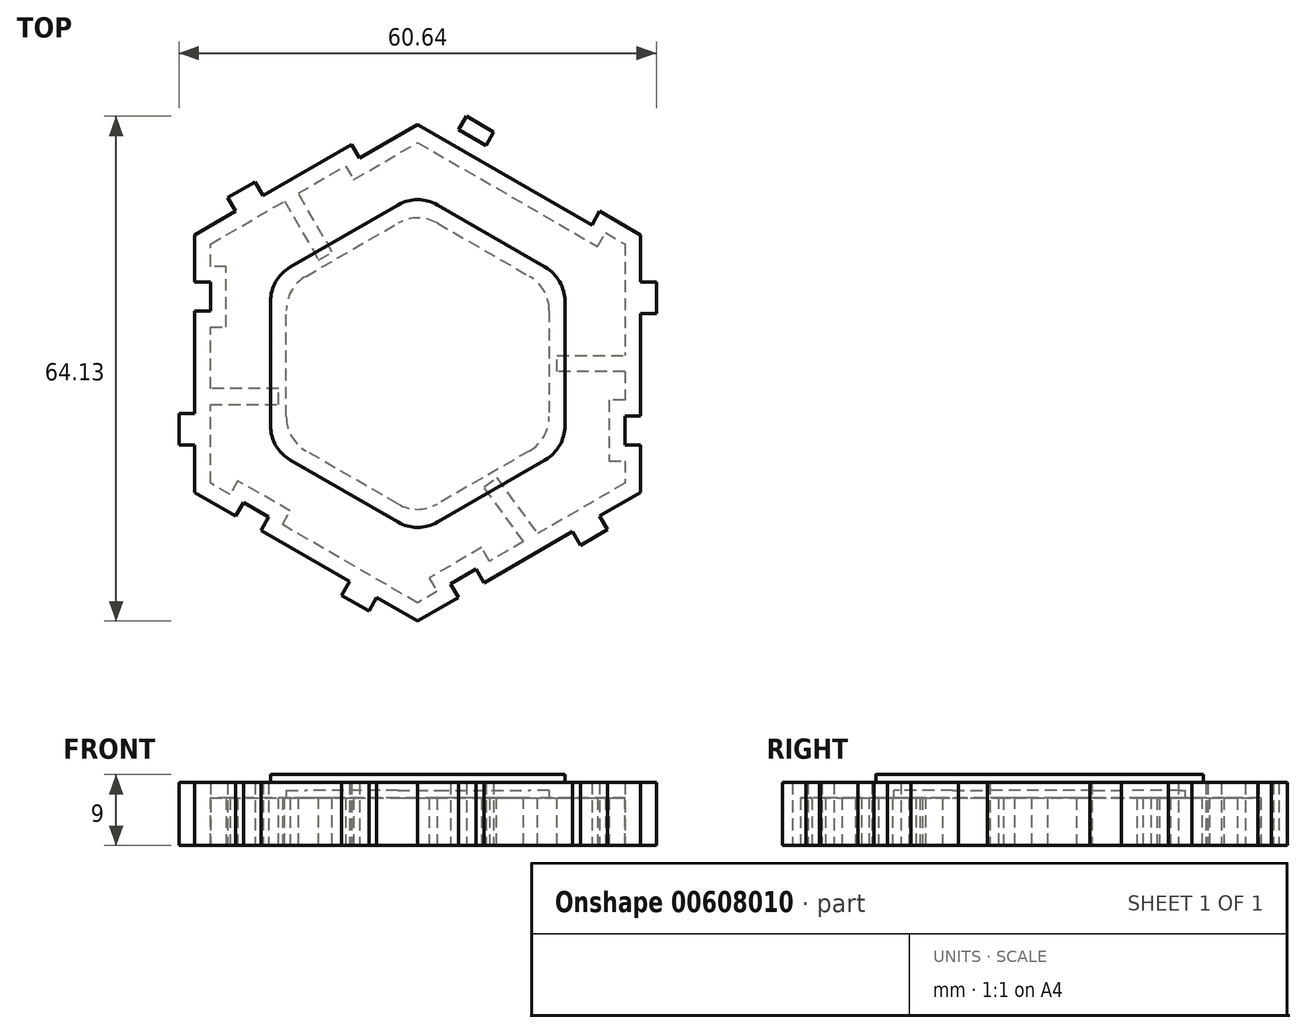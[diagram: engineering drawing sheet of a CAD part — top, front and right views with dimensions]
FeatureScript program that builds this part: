
annotation { "Feature Type Name" : "Feature", "Feature Type Description" : "" }
export const myFeature = defineFeature(function(context is Context, id is Id, definition is map)
    precondition{}
    {
        {
            var Q0;
            Q0=qCreatedBy(makeId("Top.planeOp"),FACE);
            var sketch = newSketch(context, id + "F0", { "sketchPlane" : qUnion([Q0])});
            skCircle(sketch, "E0.cCircle", {"center": v(0, 0) * mm, "radius": 18.7 * mm, "construction": true});
            skLineSegment(sketch, "E0.0", {"start": v(-18.7, -10.8) * mm, "end": v(-18.7, 10.8) * mm});
            skLineSegment(sketch, "E0.1", {"start": v(-18.7, 10.8) * mm, "end": v(0, 21.6) * mm});
            skLineSegment(sketch, "E0.2", {"start": v(0, 21.6) * mm, "end": v(18.7, 10.8) * mm});
            skLineSegment(sketch, "E0.3", {"start": v(18.7, 10.8) * mm, "end": v(18.7, -10.8) * mm});
            skLineSegment(sketch, "E0.4", {"start": v(18.7, -10.8) * mm, "end": v(0, -21.6) * mm});
            skLineSegment(sketch, "E0.5", {"start": v(0, -21.6) * mm, "end": v(-18.7, -10.8) * mm});
            skPoint(sketch, "E0.0.midPoint", {"position": v(-18.7, 0) * mm});
            skLineSegment(sketch, "E1.0", {"start": v(-26.32, 15.2) * mm, "end": v(0, 30.39) * mm});
            skLineSegment(sketch, "E1.1", {"start": v(26.32, 15.2) * mm, "end": v(26.32, -15.2) * mm});
            skLineSegment(sketch, "E1.2", {"start": v(26.32, -15.2) * mm, "end": v(0, -30.39) * mm});
            skLineSegment(sketch, "E1.3", {"start": v(0, 30.39) * mm, "end": v(26.32, 15.2) * mm});
            skLineSegment(sketch, "E1.4", {"start": v(0, -30.39) * mm, "end": v(-26.32, -15.2) * mm});
            skLineSegment(sketch, "E1.5", {"start": v(-26.32, -15.2) * mm, "end": v(-26.32, 15.2) * mm});
            skLineSegment(sketch, "E2.0", {"start": v(-28.32, 16.35) * mm, "end": v(0, 32.7) * mm});
            skLineSegment(sketch, "E2.1", {"start": v(28.32, 16.35) * mm, "end": v(28.32, -16.35) * mm});
            skLineSegment(sketch, "E2.2", {"start": v(28.32, -16.35) * mm, "end": v(0, -32.7) * mm});
            skLineSegment(sketch, "E2.3", {"start": v(0, 32.7) * mm, "end": v(28.32, 16.35) * mm});
            skLineSegment(sketch, "E2.4", {"start": v(0, -32.7) * mm, "end": v(-28.32, -16.35) * mm});
            skLineSegment(sketch, "E2.5", {"start": v(-28.32, -16.35) * mm, "end": v(-28.32, 16.35) * mm});
            skLineSegment(sketch, "E3", {"start": v(-23.12, 19.35) * mm, "end": v(-24.12, 21.08) * mm});
            skLineSegment(sketch, "E4", {"start": v(-24.12, 21.08) * mm, "end": v(-20.66, 23.08) * mm});
            skLineSegment(sketch, "E5", {"start": v(-20.66, 23.08) * mm, "end": v(-19.66, 21.35) * mm});
            skLineSegment(sketch, "E6", {"start": v(-8.4, 27.85) * mm, "end": v(-7.4, 26.12) * mm});
            skLineSegment(sketch, "E7", {"start": v(-7.4, 26.12) * mm, "end": v(-4.2, 27.97) * mm});
            skLineSegment(sketch, "E8", {"start": v(-4.2, 27.97) * mm, "end": v(-5.2, 29.7) * mm});
            skLineSegment(sketch, "E9.1.0", {"start": v(30.32, 10.35) * mm, "end": v(30.32, 6.35) * mm});
            skLineSegment(sketch, "E9.1.1", {"start": v(30.32, 6.35) * mm, "end": v(28.32, 6.35) * mm});
            skLineSegment(sketch, "E9.1.2", {"start": v(28.32, -6.65) * mm, "end": v(26.32, -6.65) * mm});
            skLineSegment(sketch, "E9.1.3", {"start": v(26.32, -10.35) * mm, "end": v(28.32, -10.35) * mm});
            skLineSegment(sketch, "E9.1.4", {"start": v(28.32, 10.35) * mm, "end": v(30.32, 10.35) * mm});
            skLineSegment(sketch, "E9.2.0", {"start": v(-6.2, -31.43) * mm, "end": v(-9.66, -29.43) * mm});
            skLineSegment(sketch, "E9.2.1", {"start": v(-9.66, -29.43) * mm, "end": v(-8.66, -27.7) * mm});
            skLineSegment(sketch, "E9.2.2", {"start": v(-19.92, -21.2) * mm, "end": v(-18.92, -19.47) * mm});
            skLineSegment(sketch, "E9.2.3", {"start": v(-22.12, -17.62) * mm, "end": v(-23.12, -19.35) * mm});
            skLineSegment(sketch, "E9.2.4", {"start": v(-5.2, -29.7) * mm, "end": v(-6.2, -31.43) * mm});
            skLineSegment(sketch, "E9.anchor1", {"start": v(0, 0) * mm, "end": v(-24.12, 21.08) * mm, "construction": true});
            skLineSegment(sketch, "E9.anchor2", {"start": v(0, 0) * mm, "end": v(-6.2, -31.43) * mm, "construction": true});
            skLineSegment(sketch, "E10.1.0", {"start": v(-30.32, -6.35) * mm, "end": v(-28.32, -6.35) * mm});
            skLineSegment(sketch, "E10.1.1", {"start": v(-30.32, -10.35) * mm, "end": v(-30.32, -6.35) * mm});
            skLineSegment(sketch, "E10.1.2", {"start": v(-28.32, -10.35) * mm, "end": v(-30.32, -10.35) * mm});
            skLineSegment(sketch, "E10.1.3", {"start": v(-28.32, 6.65) * mm, "end": v(-26.32, 6.65) * mm});
            skLineSegment(sketch, "E10.1.4", {"start": v(-26.32, 10.35) * mm, "end": v(-28.32, 10.35) * mm});
            skLineSegment(sketch, "E10.anchor1", {"start": v(0, 0) * mm, "end": v(-9.66, -29.43) * mm, "construction": true});
            skLineSegment(sketch, "E10.anchor2", {"start": v(0, 0) * mm, "end": v(-20.66, 23.08) * mm, "construction": true});
            skLineSegment(sketch, "E11.1.0", {"start": v(23.12, -19.35) * mm, "end": v(24.12, -21.08) * mm});
            skLineSegment(sketch, "E11.1.1", {"start": v(20.66, -23.08) * mm, "end": v(19.66, -21.35) * mm});
            skLineSegment(sketch, "E11.1.2", {"start": v(24.12, -21.08) * mm, "end": v(20.66, -23.08) * mm});
            skLineSegment(sketch, "E11.1.3", {"start": v(8.4, -27.85) * mm, "end": v(7.4, -26.12) * mm});
            skLineSegment(sketch, "E11.1.4", {"start": v(4.2, -27.97) * mm, "end": v(5.2, -29.7) * mm});
            skLineSegment(sketch, "E11.anchor1", {"start": v(0, 0) * mm, "end": v(28.32, 10.35) * mm, "construction": true});
            skLineSegment(sketch, "E11.anchor2", {"start": v(0, 0) * mm, "end": v(-5.2, -29.7) * mm, "construction": true});
            skLineSegment(sketch, "E12.1.0", {"start": v(22.12, 17.62) * mm, "end": v(23.12, 19.35) * mm});
            skLineSegment(sketch, "E12.1.1", {"start": v(19.92, 21.2) * mm, "end": v(18.92, 19.47) * mm});
            skLineSegment(sketch, "E12.1.2", {"start": v(9.66, 29.43) * mm, "end": v(8.66, 27.7) * mm});
            skLineSegment(sketch, "E12.1.3", {"start": v(6.2, 31.43) * mm, "end": v(9.66, 29.43) * mm});
            skLineSegment(sketch, "E12.1.4", {"start": v(5.2, 29.7) * mm, "end": v(6.2, 31.43) * mm});
            skLineSegment(sketch, "E12.anchor1", {"start": v(0, 0) * mm, "end": v(-28.32, 10.35) * mm, "construction": true});
            skLineSegment(sketch, "E12.anchor2", {"start": v(0, 0) * mm, "end": v(5.2, -29.7) * mm, "construction": true});
            skSolve(sketch);
        }
        {
            var Q0;
            {var subQ0=sQuery(id+"F0.wireOp",EDGE,"E3");Q0=makeQuery(id+"F0.imprint","IMPRINT",FACE,{"disambiguationData":[TD([[makeQuery(id+"F0.imprint","IMPRINT",EDGE,{"derivedFrom":subQ0}),-1.0]])]});}
            var Q1;
            Q1=makeQuery(id+"F0.imprint","IMPRINT",FACE,{"disambiguationData":[TD([[makeQuery(id+"F0.imprint","IMPRINT",EDGE,{"derivedFrom":sQuery(id+"F0.wireOp",EDGE,"E0.0")}),1.0]])]});
            var Q2;
            Q2=makeQuery(id+"F0.imprint","IMPRINT",FACE,{"disambiguationData":[TD([[makeQuery(id+"F0.imprint","IMPRINT",EDGE,{"derivedFrom":sQuery(id+"F0.wireOp",EDGE,"E9.2.0")}),-1.0]])]});
            var Q3;
            Q3=makeQuery(id+"F0.imprint","IMPRINT",FACE,{"disambiguationData":[TD([[makeQuery(id+"F0.imprint","IMPRINT",EDGE,{"derivedFrom":sQuery(id+"F0.wireOp",EDGE,"E9.1.0")}),-1.0]])]});
            var Q4;
            {var subQ0=sQuery(id+"F0.wireOp",EDGE,"E10.1.0");Q4=makeQuery(id+"F0.imprint","IMPRINT",FACE,{"disambiguationData":[TD([[makeQuery(id+"F0.imprint","IMPRINT",EDGE,{"derivedFrom":subQ0}),-1.0]])]});}
            var Q5;
            {var subQ9=sQuery(id+"F0.wireOp",EDGE,"E9.2.3");Q5=makeQuery(id+"F0.imprint","IMPRINT",FACE,{"disambiguationData":[TD([[makeQuery(id+"F0.imprint","IMPRINT",EDGE,{"derivedFrom":subQ9}),-1.0]])]});}
            var Q6;
            {var subQ8=sQuery(id+"F0.wireOp",EDGE,"E10.1.4");Q6=makeQuery(id+"F0.imprint","IMPRINT",FACE,{"disambiguationData":[TD([[makeQuery(id+"F0.imprint","IMPRINT",EDGE,{"derivedFrom":subQ8}),-1.0]])]});}
            var Q7;
            {var subQ0=sQuery(id+"F0.wireOp",EDGE,"E5");Q7=makeQuery(id+"F0.imprint","IMPRINT",FACE,{"disambiguationData":[TD([[makeQuery(id+"F0.imprint","IMPRINT",EDGE,{"derivedFrom":subQ0}),-1.0]])]});}
            var Q8;
            {var subQ7=sQuery(id+"F0.wireOp",EDGE,"E10.1.3");Q8=makeQuery(id+"F0.imprint","IMPRINT",FACE,{"disambiguationData":[TD([[makeQuery(id+"F0.imprint","IMPRINT",EDGE,{"derivedFrom":subQ7}),-1.0]])]});}
            var Q9;
            {var subQ8=sQuery(id+"F0.wireOp",EDGE,"E11.1.4");Q9=makeQuery(id+"F0.imprint","IMPRINT",FACE,{"disambiguationData":[TD([[makeQuery(id+"F0.imprint","IMPRINT",EDGE,{"derivedFrom":subQ8}),-1.0]])]});}
            var Q10;
            {var subQ0=sQuery(id+"F0.wireOp",EDGE,"E9.2.4");Q10=makeQuery(id+"F0.imprint","IMPRINT",FACE,{"disambiguationData":[TD([[makeQuery(id+"F0.imprint","IMPRINT",EDGE,{"derivedFrom":subQ0}),-1.0]])]});}
            var Q11;
            {var subQ9=sQuery(id+"F0.wireOp",EDGE,"E9.1.3");Q11=makeQuery(id+"F0.imprint","IMPRINT",FACE,{"disambiguationData":[TD([[makeQuery(id+"F0.imprint","IMPRINT",EDGE,{"derivedFrom":subQ9}),-1.0]])]});}
            var Q12;
            {var subQ0=sQuery(id+"F0.wireOp",EDGE,"E11.1.0");Q12=makeQuery(id+"F0.imprint","IMPRINT",FACE,{"disambiguationData":[TD([[makeQuery(id+"F0.imprint","IMPRINT",EDGE,{"derivedFrom":subQ0}),-1.0]])]});}
            var Q13;
            {var subQ4=sQuery(id+"F0.wireOp",EDGE,"E8");Q13=makeQuery(id+"F0.imprint","IMPRINT",FACE,{"disambiguationData":[TD([[makeQuery(id+"F0.imprint","IMPRINT",EDGE,{"derivedFrom":subQ4}),-1.0]])]});}
            var Q14;
            {var subQ0=sQuery(id+"F0.wireOp",EDGE,"E12.1.2");Q14=makeQuery(id+"F0.imprint","IMPRINT",FACE,{"disambiguationData":[TD([[makeQuery(id+"F0.imprint","IMPRINT",EDGE,{"derivedFrom":subQ0}),-1.0]])]});}
            var Q15;
            {var subQ9=sQuery(id+"F0.wireOp",EDGE,"E9.1.2");Q15=makeQuery(id+"F0.imprint","IMPRINT",FACE,{"disambiguationData":[TD([[makeQuery(id+"F0.imprint","IMPRINT",EDGE,{"derivedFrom":subQ9}),-1.0]])]});}
            var Q16;
            {var subQ7=sQuery(id+"F0.wireOp",EDGE,"E9.2.2");Q16=makeQuery(id+"F0.imprint","IMPRINT",FACE,{"disambiguationData":[TD([[makeQuery(id+"F0.imprint","IMPRINT",EDGE,{"derivedFrom":subQ7}),-1.0]])]});}
            var Q17;
            {var subQ0=sQuery(id+"F0.wireOp",EDGE,"E11.1.1");Q17=makeQuery(id+"F0.imprint","IMPRINT",FACE,{"disambiguationData":[TD([[makeQuery(id+"F0.imprint","IMPRINT",EDGE,{"derivedFrom":subQ0}),-1.0]])]});}
            extrude(context, id + "F1", {"entities" : qUnion([Q0, Q1, Q2, Q3, Q4, Q5, Q6, Q7, Q8, Q9, Q10, Q11, Q12, Q13, Q14, Q15, Q16, Q17]), "depth" : 8 * mm, "offsetDistance" : 25 * mm});
        }
        {
            var Q0;
            Q0=makeQuery(id+"F0.imprint","IMPRINT",FACE,{"disambiguationData":[TD([[makeQuery(id+"F0.imprint","IMPRINT",EDGE,{"derivedFrom":sQuery(id+"F0.wireOp",EDGE,"E0.0")}),-1.0]])]});
            extrude(context, id + "F2", {"entities" : qUnion([Q0]), "operationType" : NewBodyOperationType.ADD, "depth" : 9 * mm, "offsetDistance" : 25 * mm});
        }
        {
            var Q0;
            {var subQ0=sQuery(id+"F0.wireOp",EDGE,"E0.5");var subQ1=sQuery(id+"F0.wireOp",EDGE,"E0.4");var subQ2=sQuery(id+"F0.wireOp",EDGE,"E0.3");var subQ3=sQuery(id+"F0.wireOp",EDGE,"E0.2");var subQ4=sQuery(id+"F0.wireOp",EDGE,"E0.1");var subQ5=sQuery(id+"F0.wireOp",EDGE,"E0.0");Q0=makeQuery(id+"F2.boolean.opBoolean","MERGE",FACE,{"derivedFrom":[makeQuery(id+"F1.opExtrude","CAP_FACE",FACE,{"disambiguationData":[OSD([subQ5,subQ4,subQ3,subQ2,subQ1,subQ0,sQuery(id+"F0.wireOp",EDGE,"E1.1"),sQuery(id+"F0.wireOp",EDGE,"E1.2"),sQuery(id+"F0.wireOp",EDGE,"E1.3"),sQuery(id+"F0.wireOp",EDGE,"E1.4"),sQuery(id+"F0.wireOp",EDGE,"E1.5"),sQuery(id+"F0.wireOp",EDGE,"E2.0"),sQuery(id+"F0.wireOp",EDGE,"E2.1"),sQuery(id+"F0.wireOp",EDGE,"E2.2"),sQuery(id+"F0.wireOp",EDGE,"E2.3"),sQuery(id+"F0.wireOp",EDGE,"E2.4"),sQuery(id+"F0.wireOp",EDGE,"E2.5"),sQuery(id+"F0.wireOp",EDGE,"E7"),sQuery(id+"F0.wireOp",EDGE,"E9.1.0"),sQuery(id+"F0.wireOp",EDGE,"E9.1.1"),sQuery(id+"F0.wireOp",EDGE,"E9.1.2"),sQuery(id+"F0.wireOp",EDGE,"E9.1.3"),sQuery(id+"F0.wireOp",EDGE,"E9.1.4"),sQuery(id+"F0.wireOp",EDGE,"E10.1.0"),sQuery(id+"F0.wireOp",EDGE,"E10.1.1"),sQuery(id+"F0.wireOp",EDGE,"E10.1.2"),sQuery(id+"F0.wireOp",EDGE,"E10.1.3"),sQuery(id+"F0.wireOp",EDGE,"E10.1.4"),sQuery(id+"F0.wireOp",EDGE,"E5"),sQuery(id+"F0.wireOp",EDGE,"E4"),sQuery(id+"F0.wireOp",EDGE,"E3"),sQuery(id+"F0.wireOp",EDGE,"E6"),sQuery(id+"F0.wireOp",EDGE,"E8"),sQuery(id+"F0.wireOp",EDGE,"E9.2.4"),sQuery(id+"F0.wireOp",EDGE,"E9.2.1"),sQuery(id+"F0.wireOp",EDGE,"E9.2.0"),sQuery(id+"F0.wireOp",EDGE,"E9.2.2"),sQuery(id+"F0.wireOp",EDGE,"E9.2.3"),sQuery(id+"F0.wireOp",EDGE,"E12.1.0"),sQuery(id+"F0.wireOp",EDGE,"E12.1.1"),sQuery(id+"F0.wireOp",EDGE,"E12.1.2"),sQuery(id+"F0.wireOp",EDGE,"E12.1.3"),sQuery(id+"F0.wireOp",EDGE,"E12.1.4"),sQuery(id+"F0.wireOp",EDGE,"E11.1.4"),sQuery(id+"F0.wireOp",EDGE,"E11.1.3"),sQuery(id+"F0.wireOp",EDGE,"E11.1.1"),sQuery(id+"F0.wireOp",EDGE,"E11.1.2"),sQuery(id+"F0.wireOp",EDGE,"E11.1.0")])],"isStart":true}),makeQuery(id+"F2.opExtrude","CAP_FACE",FACE,{"disambiguationData":[OSD([subQ5,subQ4,subQ3,subQ2,subQ1,subQ0])],"isStart":true})]});}
            shell(context, id + "F3", {"entities" : qUnion([Q0]), "thickness" : 2 * mm});
        }
        {
            var Q0;
            Q0=makeQuery(id+"F2.opExtrude","SWEPT_EDGE",EDGE,{"disambiguationData":[OSD([sQuery(id+"F0.wireOp",EDGE,"E0.0"),sQuery(id+"F0.wireOp",EDGE,"E0.1")])]});
            var Q1;
            Q1=makeQuery(id+"F2.opExtrude","SWEPT_EDGE",EDGE,{"disambiguationData":[OSD([sQuery(id+"F0.wireOp",EDGE,"E0.0"),sQuery(id+"F0.wireOp",EDGE,"E0.5")])]});
            var Q2;
            Q2=makeQuery(id+"F2.opExtrude","SWEPT_EDGE",EDGE,{"disambiguationData":[OSD([sQuery(id+"F0.wireOp",EDGE,"E0.4"),sQuery(id+"F0.wireOp",EDGE,"E0.5")])]});
            var Q3;
            Q3=makeQuery(id+"F2.opExtrude","SWEPT_EDGE",EDGE,{"disambiguationData":[OSD([sQuery(id+"F0.wireOp",EDGE,"E0.3"),sQuery(id+"F0.wireOp",EDGE,"E0.4")])]});
            var Q4;
            Q4=makeQuery(id+"F2.opExtrude","SWEPT_EDGE",EDGE,{"disambiguationData":[OSD([sQuery(id+"F0.wireOp",EDGE,"E0.2"),sQuery(id+"F0.wireOp",EDGE,"E0.3")])]});
            var Q5;
            Q5=makeQuery(id+"F2.opExtrude","SWEPT_EDGE",EDGE,{"disambiguationData":[OSD([sQuery(id+"F0.wireOp",EDGE,"E0.1"),sQuery(id+"F0.wireOp",EDGE,"E0.2")])]});
            fillet(context, id + "F4", {"entities" : qUnion([Q0, Q1, Q2, Q3, Q4, Q5]), "radius" : 5 * mm, "tangentPropagation" : true, "allowEdgeOverflow" : false});
        }
        {
            var Q0;
            Q0=makeQuery(id+"F3.opShell","OFFSET_EDGE",EDGE,{"disambiguationData":[OSD([sQuery(id+"F0.wireOp",EDGE,"E0.1"),sQuery(id+"F0.wireOp",EDGE,"E0.2")])]});
            var Q1;
            Q1=makeQuery(id+"F3.opShell","OFFSET_EDGE",EDGE,{"disambiguationData":[OSD([sQuery(id+"F0.wireOp",EDGE,"E0.0"),sQuery(id+"F0.wireOp",EDGE,"E0.1")])]});
            var Q2;
            Q2=makeQuery(id+"F3.opShell","OFFSET_EDGE",EDGE,{"disambiguationData":[OSD([sQuery(id+"F0.wireOp",EDGE,"E0.0"),sQuery(id+"F0.wireOp",EDGE,"E0.5")])]});
            var Q3;
            Q3=makeQuery(id+"F3.opShell","OFFSET_EDGE",EDGE,{"disambiguationData":[OSD([sQuery(id+"F0.wireOp",EDGE,"E0.4"),sQuery(id+"F0.wireOp",EDGE,"E0.5")])]});
            var Q4;
            Q4=makeQuery(id+"F3.opShell","OFFSET_EDGE",EDGE,{"disambiguationData":[OSD([sQuery(id+"F0.wireOp",EDGE,"E0.3"),sQuery(id+"F0.wireOp",EDGE,"E0.4")])]});
            var Q5;
            Q5=makeQuery(id+"F3.opShell","OFFSET_EDGE",EDGE,{"disambiguationData":[OSD([sQuery(id+"F0.wireOp",EDGE,"E0.2"),sQuery(id+"F0.wireOp",EDGE,"E0.3")])]});
            fillet(context, id + "F5", {"entities" : qUnion([Q0, Q1, Q2, Q3, Q4, Q5]), "radius" : 5 * mm, "tangentPropagation" : true, "allowEdgeOverflow" : false});
        }
        {
            var Q0;
            Q0=makeQuery(id+"F3.opShell","OFFSET_FACE",FACE,{"disambiguationData":[OSD([sQuery(id+"F0.wireOp",EDGE,"E0.0"),sQuery(id+"F0.wireOp",EDGE,"E0.1"),sQuery(id+"F0.wireOp",EDGE,"E0.2"),sQuery(id+"F0.wireOp",EDGE,"E0.3"),sQuery(id+"F0.wireOp",EDGE,"E0.4"),sQuery(id+"F0.wireOp",EDGE,"E0.5"),sQuery(id+"F0.wireOp",EDGE,"E1.1"),sQuery(id+"F0.wireOp",EDGE,"E1.2"),sQuery(id+"F0.wireOp",EDGE,"E1.3"),sQuery(id+"F0.wireOp",EDGE,"E1.4"),sQuery(id+"F0.wireOp",EDGE,"E1.5"),sQuery(id+"F0.wireOp",EDGE,"E2.0"),sQuery(id+"F0.wireOp",EDGE,"E2.1"),sQuery(id+"F0.wireOp",EDGE,"E2.2"),sQuery(id+"F0.wireOp",EDGE,"E2.3"),sQuery(id+"F0.wireOp",EDGE,"E2.4"),sQuery(id+"F0.wireOp",EDGE,"E2.5"),sQuery(id+"F0.wireOp",EDGE,"E7"),sQuery(id+"F0.wireOp",EDGE,"E9.1.0"),sQuery(id+"F0.wireOp",EDGE,"E9.1.1"),sQuery(id+"F0.wireOp",EDGE,"E9.1.2"),sQuery(id+"F0.wireOp",EDGE,"E9.1.3"),sQuery(id+"F0.wireOp",EDGE,"E9.1.4"),sQuery(id+"F0.wireOp",EDGE,"E10.1.0"),sQuery(id+"F0.wireOp",EDGE,"E10.1.1"),sQuery(id+"F0.wireOp",EDGE,"E10.1.2"),sQuery(id+"F0.wireOp",EDGE,"E10.1.3"),sQuery(id+"F0.wireOp",EDGE,"E10.1.4"),sQuery(id+"F0.wireOp",EDGE,"E5"),sQuery(id+"F0.wireOp",EDGE,"E4"),sQuery(id+"F0.wireOp",EDGE,"E3"),sQuery(id+"F0.wireOp",EDGE,"E6"),sQuery(id+"F0.wireOp",EDGE,"E8"),sQuery(id+"F0.wireOp",EDGE,"E9.2.4"),sQuery(id+"F0.wireOp",EDGE,"E9.2.1"),sQuery(id+"F0.wireOp",EDGE,"E9.2.0"),sQuery(id+"F0.wireOp",EDGE,"E9.2.2"),sQuery(id+"F0.wireOp",EDGE,"E9.2.3"),sQuery(id+"F0.wireOp",EDGE,"E12.1.0"),sQuery(id+"F0.wireOp",EDGE,"E12.1.1"),sQuery(id+"F0.wireOp",EDGE,"E12.1.2"),sQuery(id+"F0.wireOp",EDGE,"E12.1.3"),sQuery(id+"F0.wireOp",EDGE,"E12.1.4"),sQuery(id+"F0.wireOp",EDGE,"E11.1.4"),sQuery(id+"F0.wireOp",EDGE,"E11.1.3"),sQuery(id+"F0.wireOp",EDGE,"E11.1.1"),sQuery(id+"F0.wireOp",EDGE,"E11.1.2"),sQuery(id+"F0.wireOp",EDGE,"E11.1.0")])]});
            var sketch = newSketch(context, id + "F6", { "sketchPlane" : qUnion([Q0])});
            skLineSegment(sketch, "E13", {"start": v(13.46, 22.62) * mm, "end": v(8.4, 15.66) * mm});
            skLineSegment(sketch, "E14", {"start": v(8.4, 15.66) * mm, "end": v(10.01, 14.49) * mm});
            skLineSegment(sketch, "E15", {"start": v(10.01, 14.49) * mm, "end": v(15.2, 21.61) * mm});
            skLineSegment(sketch, "E16", {"start": v(-16.9, -20.64) * mm, "end": v(-12.58, -13.17) * mm});
            skLineSegment(sketch, "E17", {"start": v(-12.58, -13.17) * mm, "end": v(-10.85, -14.17) * mm});
            skLineSegment(sketch, "E18", {"start": v(-10.85, -14.17) * mm, "end": v(-15.16, -21.64) * mm});
            skLineSegment(sketch, "E19", {"start": v(-26.32, 5.18) * mm, "end": v(-17.7, 5.18) * mm});
            skLineSegment(sketch, "E20", {"start": v(-17.7, 5.18) * mm, "end": v(-17.7, 3.18) * mm});
            skLineSegment(sketch, "E21", {"start": v(-17.7, 3.18) * mm, "end": v(-26.32, 3.18) * mm});
            skLineSegment(sketch, "E22", {"start": v(26.32, 1) * mm, "end": v(17.7, 1) * mm});
            skLineSegment(sketch, "E23", {"start": v(17.7, 1) * mm, "end": v(17.7, -1) * mm});
            skLineSegment(sketch, "E24", {"start": v(17.7, -1) * mm, "end": v(26.32, -1) * mm});
            skSolve(sketch);
        }
        {
            var Q0;
            {var subQ0=sQuery(id+"F6.wireOp",EDGE,"E13");Q0=makeQuery(id+"F6.imprint","IMPRINT",FACE,{"disambiguationData":[TD([[makeQuery(id+"F6.imprint","IMPRINT",EDGE,{"derivedFrom":subQ0}),1.0]])]});}
            var Q1;
            {var subQ0=sQuery(id+"F6.wireOp",EDGE,"E19");Q1=makeQuery(id+"F6.imprint","IMPRINT",FACE,{"disambiguationData":[TD([[makeQuery(id+"F6.imprint","IMPRINT",EDGE,{"derivedFrom":subQ0}),-1.0]])]});}
            var Q2;
            {var subQ0=sQuery(id+"F6.wireOp",EDGE,"E22");Q2=makeQuery(id+"F6.imprint","IMPRINT",FACE,{"disambiguationData":[TD([[makeQuery(id+"F6.imprint","IMPRINT",EDGE,{"derivedFrom":subQ0}),1.0]])]});}
            var Q3;
            {var subQ0=sQuery(id+"F6.wireOp",EDGE,"E16");Q3=makeQuery(id+"F6.imprint","IMPRINT",FACE,{"disambiguationData":[TD([[makeQuery(id+"F6.imprint","IMPRINT",EDGE,{"derivedFrom":subQ0}),-1.0]])]});}
            extrude(context, id + "F7", {"entities" : qUnion([Q0, Q1, Q2, Q3]), "operationType" : NewBodyOperationType.ADD, "depth" : 6 * mm, "offsetDistance" : 25 * mm});
        }
    });
